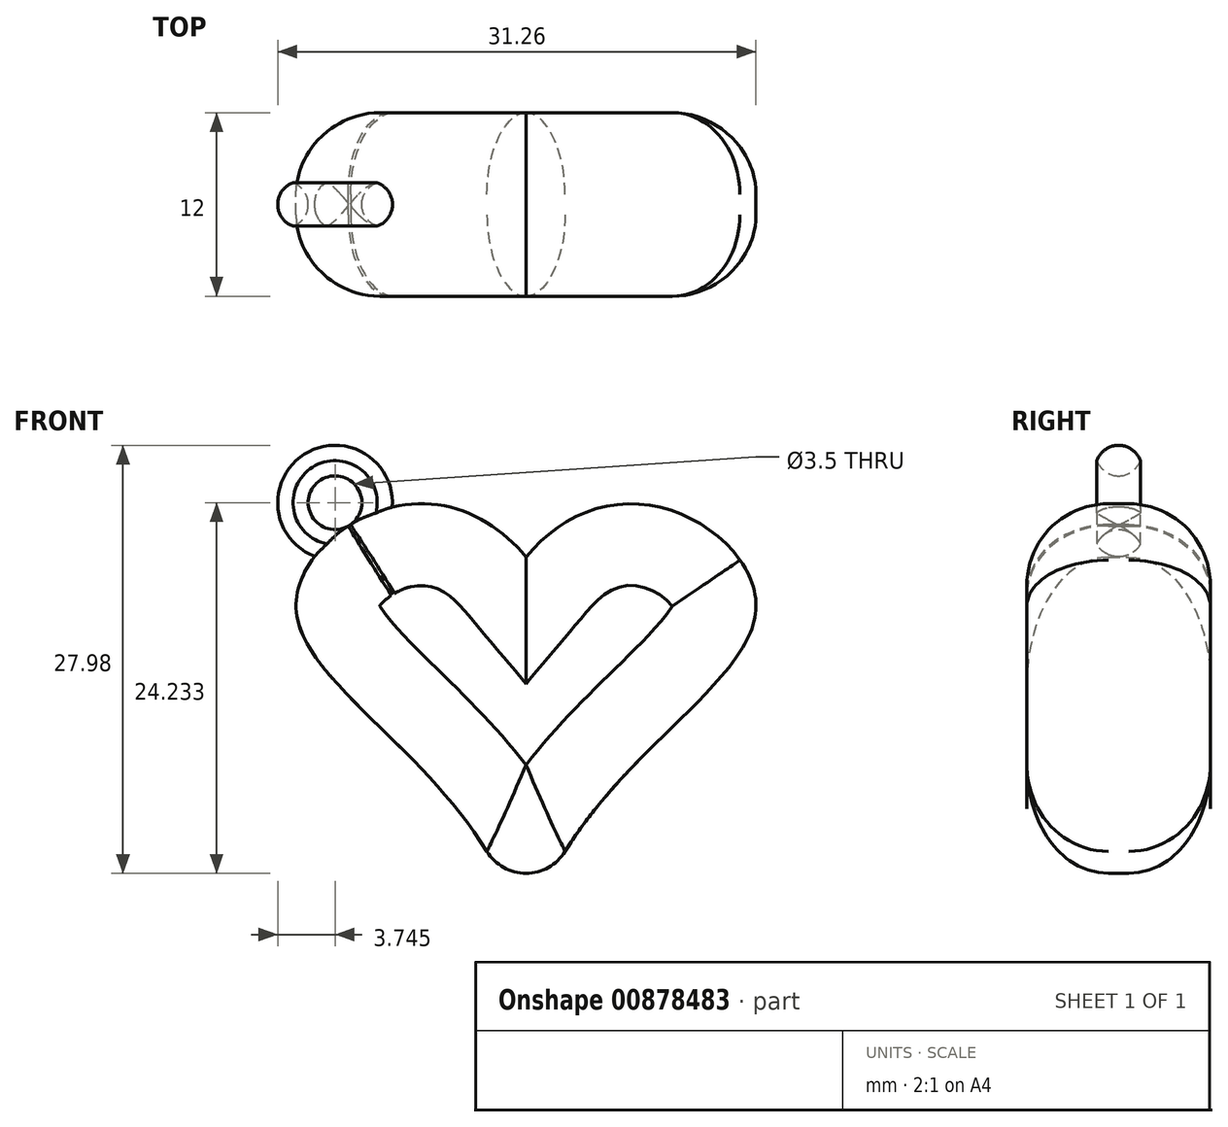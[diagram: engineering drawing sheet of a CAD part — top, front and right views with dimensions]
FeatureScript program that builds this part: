
annotation { "Feature Type Name" : "Feature", "Feature Type Description" : "" }
export const myFeature = defineFeature(function(context is Context, id is Id, definition is map)
    precondition{}
    {
        {
            var Q0;
            Q0=qCreatedBy(makeId("Front.planeOp"),FACE);
            var sketch = newSketch(context, id + "F0", { "sketchPlane" : qUnion([Q0])});
            skFitSpline(sketch, "E0", {"points": [v(0, 0) * mm, v(-15, 22.94) * mm, v(0, 25.57) * mm], "startDerivative": vector(-12.7, 61.92) * mm, "endDerivative": vector(41.8, -49.62) * mm});
            skFitSpline(sketch, "E1.MirrorCS", {"points": [v(0, 0) * mm, v(15, 22.94) * mm, v(0, 25.57) * mm], "startDerivative": vector(12.7, 61.92) * mm, "endDerivative": vector(-41.8, -49.62) * mm});
            skPoint(sketch, "E2.first.point", {"position": v(-11.58, 27.62) * mm});
            skCircle(sketch, "E3", {"center": v(-12.48, 29.12) * mm, "radius": 1.75 * mm});
            skArc(sketch, "E4", {"start": v(-8.75, 28.83) * mm, "mid": v(-14.5, 32.29) * mm, "end": v(-13.8, 25.61) * mm});
            skSolve(sketch);
        }
        {
            var Q0;
            {var subQ0=sQuery(id+"F0.wireOp",EDGE,"E2");var subQ1=sQuery(id+"F0.wireOp",EDGE,"E0");var subQ2=makeQuery(id+"F0.imprint","INTERSECT",VERTEX,{"disambiguationData":[OD(0.0)],"derivedFrom":[subQ1,subQ0]});Q0=makeQuery(id+"F0.imprint","IMPRINT",FACE,{"disambiguationData":[TD([[makeQuery(id+"F0.imprint","IMPRINT",EDGE,{"disambiguationData":[TD([[subQ2,-1.0]])],"derivedFrom":subQ1}),-1.0]])]});}
            var Q1;
            {var subQ0=sQuery(id+"F0.wireOp",EDGE,"E1.MirrorCS");Q1=makeQuery(id+"F0.imprint","IMPRINT",FACE,{"disambiguationData":[TD([[makeQuery(id+"F0.imprint","IMPRINT",EDGE,{"derivedFrom":subQ0}),1.0]])]});}
            extrude(context, id + "F1", {"entities" : qUnion([Q0, Q1]), "endBound" : BoundingType.SYMMETRIC, "depth" : 12 * mm, "offsetDistance" : 25 * mm});
        }
        {
            var Q0;
            {var subQ0=sQuery(id+"F0.wireOp",EDGE,"E4");Q0=makeQuery(id+"F0.imprint","IMPRINT",FACE,{"disambiguationData":[TD([[makeQuery(id+"F0.imprint","IMPRINT",EDGE,{"derivedFrom":subQ0}),1.0]])]});}
            extrude(context, id + "F2", {"entities" : qUnion([Q0]), "operationType" : NewBodyOperationType.ADD, "endBound" : BoundingType.SYMMETRIC, "depth" : 3 * mm, "offsetDistance" : 25 * mm});
        }
        {
            var Q0;
            Q0=makeQuery(id+"F2.opExtrude","CAP_EDGE",EDGE,{"disambiguationData":[OSD([sQuery(id+"F0.wireOp",EDGE,"E4")])],"isStart":false});
            var Q1;
            Q1=makeQuery(id+"F2.opExtrude","CAP_EDGE",EDGE,{"disambiguationData":[OSD([sQuery(id+"F0.wireOp",EDGE,"E4")])],"isStart":true});
            var Q2;
            Q2=makeQuery(id+"F2.opExtrude","CAP_EDGE",EDGE,{"disambiguationData":[OSD([sQuery(id+"F0.wireOp",EDGE,"E3")])],"isStart":true});
            var Q3;
            Q3=makeQuery(id+"F2.opExtrude","CAP_EDGE",EDGE,{"disambiguationData":[OSD([sQuery(id+"F0.wireOp",EDGE,"E3")])],"isStart":false});
            fillet(context, id + "F3", {"entities" : qUnion([Q0, Q1, Q2, Q3]), "radius" : 1.49 * mm, "tangentPropagation" : true, "allowEdgeOverflow" : false});
        }
        {
            var Q0;
            Q0=makeQuery(id+"F1.opExtrude","CAP_FACE",FACE,{"disambiguationData":[OSD([sQuery(id+"F0.wireOp",EDGE,"E0"),sQuery(id+"F0.wireOp",EDGE,"E1.MirrorCS"),sQuery(id+"F0.wireOp",EDGE,"E3")])],"isStart":false});
            var Q1;
            Q1=makeQuery(id+"F1.opExtrude","CAP_FACE",FACE,{"disambiguationData":[OSD([sQuery(id+"F0.wireOp",EDGE,"E0"),sQuery(id+"F0.wireOp",EDGE,"E1.MirrorCS"),sQuery(id+"F0.wireOp",EDGE,"E3")])],"isStart":true});
            fillet(context, id + "F4", {"entities" : qUnion([Q0, Q1]), "radius" : 5.34 * mm, "tangentPropagation" : true, "allowEdgeOverflow" : false});
        }
        {
            var Q0;
            {var subQ0=sQuery(id+"F0.wireOp",EDGE,"E1.MirrorCS");var subQ1=sQuery(id+"F0.wireOp",EDGE,"E0");var subQ2=makeQuery(id+"F0.imprint","INTERSECT",VERTEX,{"disambiguationData":[OD(1.0)],"derivedFrom":[subQ1,sQuery(id+"F0.wireOp",EDGE,"E4")]});Q0=makeQuery(id+"F4.opFillet","BLEND_EDGE",EDGE,{"blendedFrom":[makeQuery(id+"F1.opExtrude","CAP_EDGE",EDGE,{"disambiguationData":[OSD([subQ1]),TDD([makeQuery(id+"F0.imprint","IMPRINT",EDGE,{"disambiguationData":[TD([[makeQuery(id+"F0.imprint","INTERSECT",VERTEX,{"disambiguationData":[OD(0.0)],"derivedFrom":[subQ1,subQ0]}),-1.0]])],"derivedFrom":subQ1}),makeQuery(id+"F0.imprint","IMPRINT",EDGE,{"disambiguationData":[TD([[subQ2,-1.0]])],"derivedFrom":subQ1})])],"isStart":false}),makeQuery(id+"F1.opExtrude","CAP_EDGE",EDGE,{"disambiguationData":[OSD([subQ0])],"isStart":false})],"blendedInto":[]});}
            var Q1;
            {var subQ0=sQuery(id+"F0.wireOp",EDGE,"E1.MirrorCS");var subQ1=sQuery(id+"F0.wireOp",EDGE,"E0");Q1=makeQuery(id+"F1.opExtrude","SWEPT_EDGE",EDGE,{"disambiguationData":[OSD([subQ1,subQ0]),TDD([makeQuery(id+"F0.imprint","INTERSECT",VERTEX,{"disambiguationData":[OD(0.0)],"derivedFrom":[subQ1,subQ0]})])]});}
            var Q2;
            Q2=makeQuery(id+"F4.opFillet","BLEND_EDGE",EDGE,{"blendedFrom":[makeQuery(id+"F1.opExtrude","CAP_EDGE",EDGE,{"disambiguationData":[OSD([sQuery(id+"F0.wireOp",EDGE,"E1.MirrorCS")])],"isStart":true}),makeQuery(id+"F1.opExtrude","CAP_EDGE",EDGE,{"disambiguationData":[OSD([sQuery(id+"F0.wireOp",EDGE,"E3")])],"isStart":true})],"blendedInto":[]});
            fillet(context, id + "F5", {"entities" : qUnion([Q0, Q1, Q2]), "radius" : 3 * mm, "tangentPropagation" : true, "allowEdgeOverflow" : false});
        }
    });
